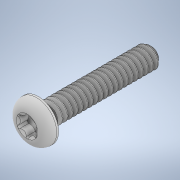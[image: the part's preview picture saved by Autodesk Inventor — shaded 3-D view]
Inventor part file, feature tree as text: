
AUTODESK INVENTOR PART (.ipt)
format: ipt  version: 2021 (Build 250183000, 183)  size: 694,784 bytes
history: native  units: in
note: dims shown in document units (in); Inventor stores cm internally (conversion verified against a paired STEP export)
features: extrude x1
ambient origin geometry x8: Origin, YZ Plane, XZ Plane, XY Plane, X Axis, Y Axis, Z Axis, Center Point
bodies: Solid1 (feature_tree)
feature tree (1):
  extrude  "Extrude16"  [1 undecoded]
note: 1 required parameter value undecoded (feature->parameter linkage not recoverable at this tier; creation-order binding heuristic only, values carry confidence <= 0.55)
